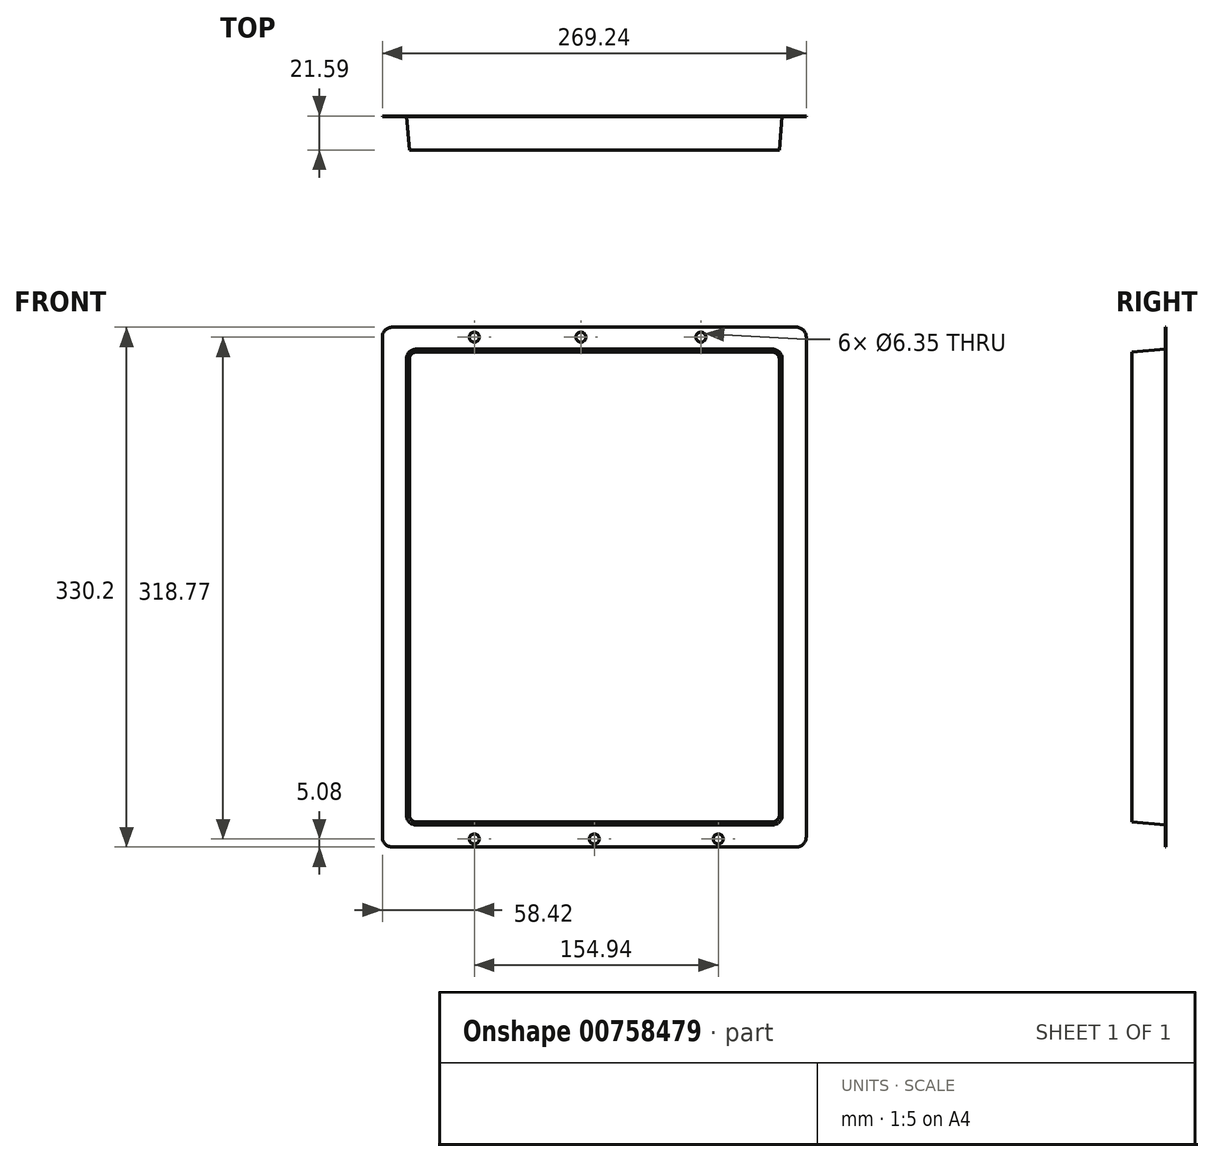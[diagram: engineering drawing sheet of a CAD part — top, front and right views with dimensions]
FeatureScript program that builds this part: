
annotation { "Feature Type Name" : "Feature", "Feature Type Description" : "" }
export const myFeature = defineFeature(function(context is Context, id is Id, definition is map)
    precondition{}
    {
        {
            var Q0;
            Q0=qCreatedBy(makeId("Front.planeOp"),FACE);
            var sketch = newSketch(context, id + "F0", { "sketchPlane" : qUnion([Q0])});
            skLineSegment(sketch, "E0.bottom", {"start": v(128.27, -165.1) * mm, "end": v(-128.27, -165.1) * mm});
            skLineSegment(sketch, "E0.top", {"start": v(128.27, 165.1) * mm, "end": v(-128.27, 165.1) * mm});
            skLineSegment(sketch, "E0.left", {"start": v(134.62, -158.75) * mm, "end": v(134.62, 158.75) * mm});
            skLineSegment(sketch, "E0.right", {"start": v(-134.62, -158.75) * mm, "end": v(-134.62, 158.75) * mm});
            skPoint(sketch, "E0.middle", {"position": v(0, 0) * mm});
            skPoint(sketch, "E1.visualSharp", {"position": v(-134.62, 165.1) * mm});
            skArc(sketch, "E1.filletArc", {"start": v(-128.27, 165.1) * mm, "mid": v(-132.76, 163.24) * mm, "end": v(-134.62, 158.75) * mm});
            skPoint(sketch, "E2.visualSharp", {"position": v(134.62, 165.1) * mm});
            skArc(sketch, "E2.filletArc", {"start": v(134.62, 158.75) * mm, "mid": v(132.76, 163.24) * mm, "end": v(128.27, 165.1) * mm});
            skPoint(sketch, "E3.visualSharp", {"position": v(134.62, -165.1) * mm});
            skArc(sketch, "E3.filletArc", {"start": v(128.27, -165.1) * mm, "mid": v(132.76, -163.24) * mm, "end": v(134.62, -158.75) * mm});
            skPoint(sketch, "E4.visualSharp", {"position": v(-134.62, -165.1) * mm});
            skArc(sketch, "E4.filletArc", {"start": v(-134.62, -158.75) * mm, "mid": v(-132.76, -163.24) * mm, "end": v(-128.27, -165.1) * mm});
            skCircle(sketch, "E5", {"center": v(67.7, 158.75) * mm, "radius": 3.18 * mm});
            skCircle(sketch, "E6", {"center": v(-76.2, 158.75) * mm, "radius": 3.18 * mm});
            skCircle(sketch, "E7", {"center": v(-8.5, 158.75) * mm, "radius": 3.18 * mm});
            skCircle(sketch, "E8", {"center": v(-76.2, -160.02) * mm, "radius": 3.18 * mm});
            skCircle(sketch, "E9", {"center": v(0, -160.02) * mm, "radius": 3.18 * mm});
            skCircle(sketch, "E10", {"center": v(78.74, -160.02) * mm, "radius": 3.18 * mm});
            skLineSegment(sketch, "E11.bottom", {"start": v(113.03, -151.13) * mm, "end": v(-113.03, -151.13) * mm});
            skLineSegment(sketch, "E11.top", {"start": v(113.03, 151.13) * mm, "end": v(-113.03, 151.13) * mm});
            skLineSegment(sketch, "E11.left", {"start": v(119.38, -144.78) * mm, "end": v(119.38, 144.78) * mm});
            skLineSegment(sketch, "E11.right", {"start": v(-119.38, -144.78) * mm, "end": v(-119.38, 144.78) * mm});
            skPoint(sketch, "E12.visualSharp", {"position": v(119.38, 151.13) * mm});
            skArc(sketch, "E12.filletArc", {"start": v(119.38, 144.78) * mm, "mid": v(117.52, 149.27) * mm, "end": v(113.03, 151.13) * mm});
            skPoint(sketch, "E13.visualSharp", {"position": v(-119.38, -151.13) * mm});
            skArc(sketch, "E13.filletArc", {"start": v(-119.38, -144.78) * mm, "mid": v(-117.52, -149.27) * mm, "end": v(-113.03, -151.13) * mm});
            skPoint(sketch, "E14.visualSharp", {"position": v(119.38, -151.13) * mm});
            skArc(sketch, "E14.filletArc", {"start": v(113.03, -151.13) * mm, "mid": v(117.52, -149.27) * mm, "end": v(119.38, -144.78) * mm});
            skPoint(sketch, "E15.visualSharp", {"position": v(-119.38, 151.13) * mm});
            skArc(sketch, "E15.filletArc", {"start": v(-113.03, 151.13) * mm, "mid": v(-117.52, 149.27) * mm, "end": v(-119.38, 144.78) * mm});
            skLineSegment(sketch, "E16.bottom", {"start": v(76.2, -151.13) * mm, "end": v(-76.2, -151.13) * mm});
            skLineSegment(sketch, "E16.top", {"start": v(76.2, 151.13) * mm, "end": v(-76.2, 151.13) * mm});
            skSolve(sketch);
        }
        {
            var Q0;
            Q0=makeQuery(id+"F0.imprint","IMPRINT",FACE,{"disambiguationData":[TD([[makeQuery(id+"F0.imprint","IMPRINT",EDGE,{"derivedFrom":sQuery(id+"F0.wireOp",EDGE,"E0.bottom")}),-1.0]])]});
            var Q1;
            Q1=makeQuery(id+"F0.imprint","IMPRINT",FACE,{"disambiguationData":[TD([[makeQuery(id+"F0.imprint","IMPRINT",EDGE,{"derivedFrom":sQuery(id+"F0.wireOp",EDGE,"1Ieq0WEa-MW6y-Ak9X-xvU8-gsL1TU5djiFP.bottom")}),-1.0]])]});
            var Q2;
            Q2=makeQuery(id+"F0.imprint","IMPRINT",FACE,{"disambiguationData":[TD([[makeQuery(id+"F0.imprint","IMPRINT",EDGE,{"derivedFrom":sQuery(id+"F0.wireOp",EDGE,"E11.bottom")}),-1.0]])]});
            var Q3;
            Q3=makeQuery(id+"F0.imprint","IMPRINT",FACE,{"disambiguationData":[TD([[makeQuery(id+"F0.imprint","IMPRINT",EDGE,{"derivedFrom":sQuery(id+"F0.wireOp",EDGE,"E16.top")}),1.0]])]});
            var Q4;
            Q4=makeQuery(id+"F0.imprint","IMPRINT",FACE,{"disambiguationData":[TD([[makeQuery(id+"F0.imprint","IMPRINT",EDGE,{"derivedFrom":sQuery(id+"F0.wireOp",EDGE,"E16.bottom")}),-1.0]])]});
            var Q5;
            Q5=makeQuery(id+"F0.imprint","IMPRINT",FACE,{"disambiguationData":[TD([[makeQuery(id+"F0.imprint","IMPRINT",EDGE,{"derivedFrom":sQuery(id+"F0.wireOp",EDGE,"E11.right")}),-1.0]])]});
            var Q6;
            {var subQ2=sQuery(id+"F0.wireOp",EDGE,"ace5c8a6-5d25-4e44-ae3e-6ffbce3a5818.trimOffspring");Q6=makeQuery(id+"F0.imprint","IMPRINT",FACE,{"disambiguationData":[TD([[makeQuery(id+"F0.imprint","IMPRINT",EDGE,{"derivedFrom":subQ2}),-1.0]])]});}
            var Q7;
            Q7=makeQuery(id+"F0.imprint","IMPRINT",FACE,{"disambiguationData":[TD([[makeQuery(id+"F0.imprint","IMPRINT",EDGE,{"derivedFrom":sQuery(id+"F0.wireOp",EDGE,"E11.left")}),1.0]])]});
            extrude(context, id + "F1", {"entities" : qUnion([Q0, Q1, Q2, Q3, Q4, Q5, Q6, Q7]), "depth" : 0.25 * mm, "offsetDistance" : 25.4 * mm});
        }
        {
            var Q0;
            Q0=makeQuery(id+"F0.imprint","IMPRINT",FACE,{"disambiguationData":[TD([[makeQuery(id+"F0.imprint","IMPRINT",EDGE,{"derivedFrom":sQuery(id+"F0.wireOp",EDGE,"E11.left")}),1.0]])]});
            extrude(context, id + "F2", {"entities" : qUnion([Q0]), "operationType" : NewBodyOperationType.ADD, "depth" : 21.59 * mm, "offsetDistance" : 25.4 * mm, "hasDraft" : true, "draftAngle" : 5 * degree, "draftPullDirection" : true});
        }
    });
